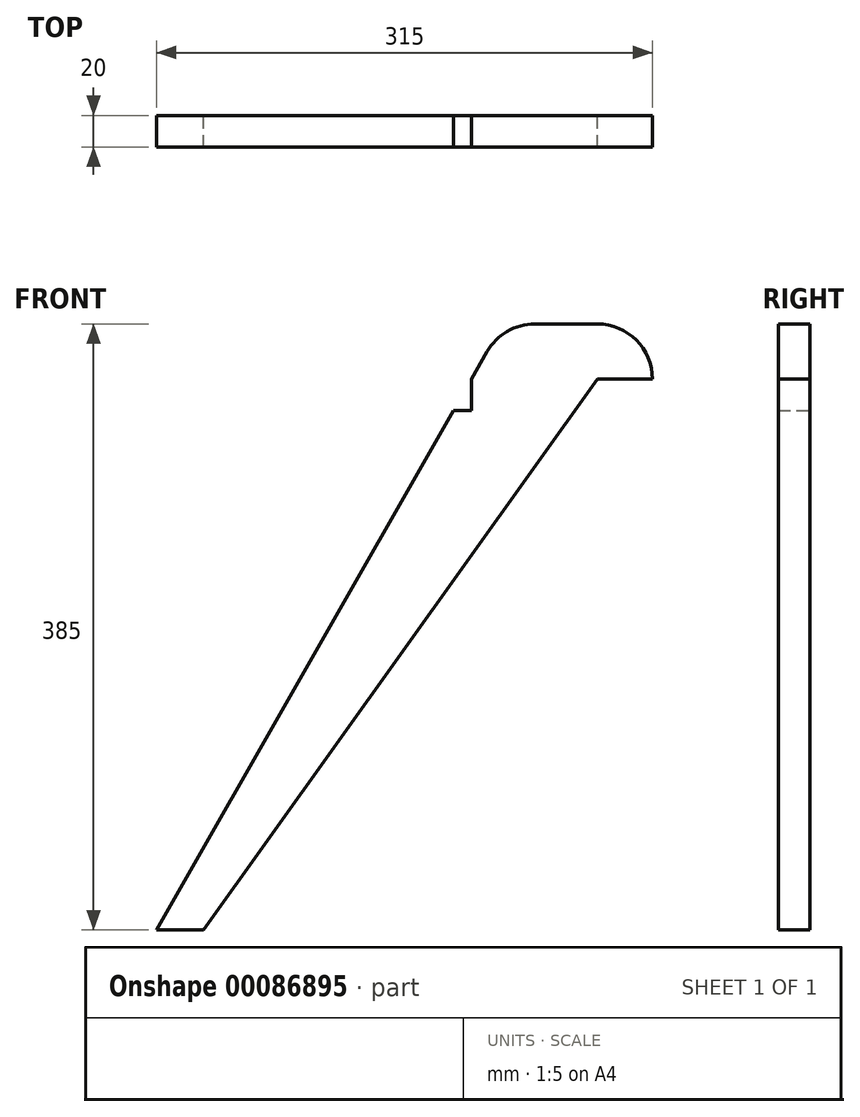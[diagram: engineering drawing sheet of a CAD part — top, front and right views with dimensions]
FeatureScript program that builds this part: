
annotation { "Feature Type Name" : "Feature", "Feature Type Description" : "" }
export const myFeature = defineFeature(function(context is Context, id is Id, definition is map)
    precondition{}
    {
        {
            var Q0;
            Q0=qCreatedBy(makeId("Front.planeOp"),FACE);
            var sketch = newSketch(context, id + "F0", { "sketchPlane" : qUnion([Q0])});
            skLineSegment(sketch, "E0", {"start": v(-30.39, 17.36) * mm, "end": v(-40.31, 0) * mm});
            skLineSegment(sketch, "E1", {"start": v(-240.31, -350) * mm, "end": v(-210.31, -350) * mm});
            skLineSegment(sketch, "E2", {"start": v(-210.31, -350) * mm, "end": v(39.69, 0) * mm});
            skLineSegment(sketch, "E3", {"start": v(39.69, 0) * mm, "end": v(74.69, 0) * mm});
            skArc(sketch, "E4", {"start": v(74.69, 0) * mm, "mid": v(64.44, 24.75) * mm, "end": v(39.69, 35) * mm});
            skPoint(sketch, "E4.centerSnap0", {"position": v(57.19, 0) * mm});
            skLineSegment(sketch, "E5", {"start": v(39.69, 35) * mm, "end": v(0, 35) * mm});
            skArc(sketch, "E6", {"start": v(0, 35) * mm, "mid": v(-17.57, 30.27) * mm, "end": v(-30.39, 17.36) * mm});
            skLineSegment(sketch, "E7.top", {"start": v(-51.74, -20) * mm, "end": v(-40.31, -20) * mm});
            skLineSegment(sketch, "E7.right", {"start": v(-40.31, 0) * mm, "end": v(-40.31, -20) * mm});
            skPoint(sketch, "E7.bottom.start.orphan", {"position": v(-137.9, 0) * mm});
            skLineSegment(sketch, "E8.trimOffspring", {"start": v(-51.74, -20) * mm, "end": v(-240.31, -350) * mm});
            skSolve(sketch);
        }
        {
            var Q0;
            Q0 = qSketchRegion(id + "F0", true);
            extrude(context, id + "F1", {"entities" : qUnion([Q0]), "depth" : 20 * mm});
        }
    });
